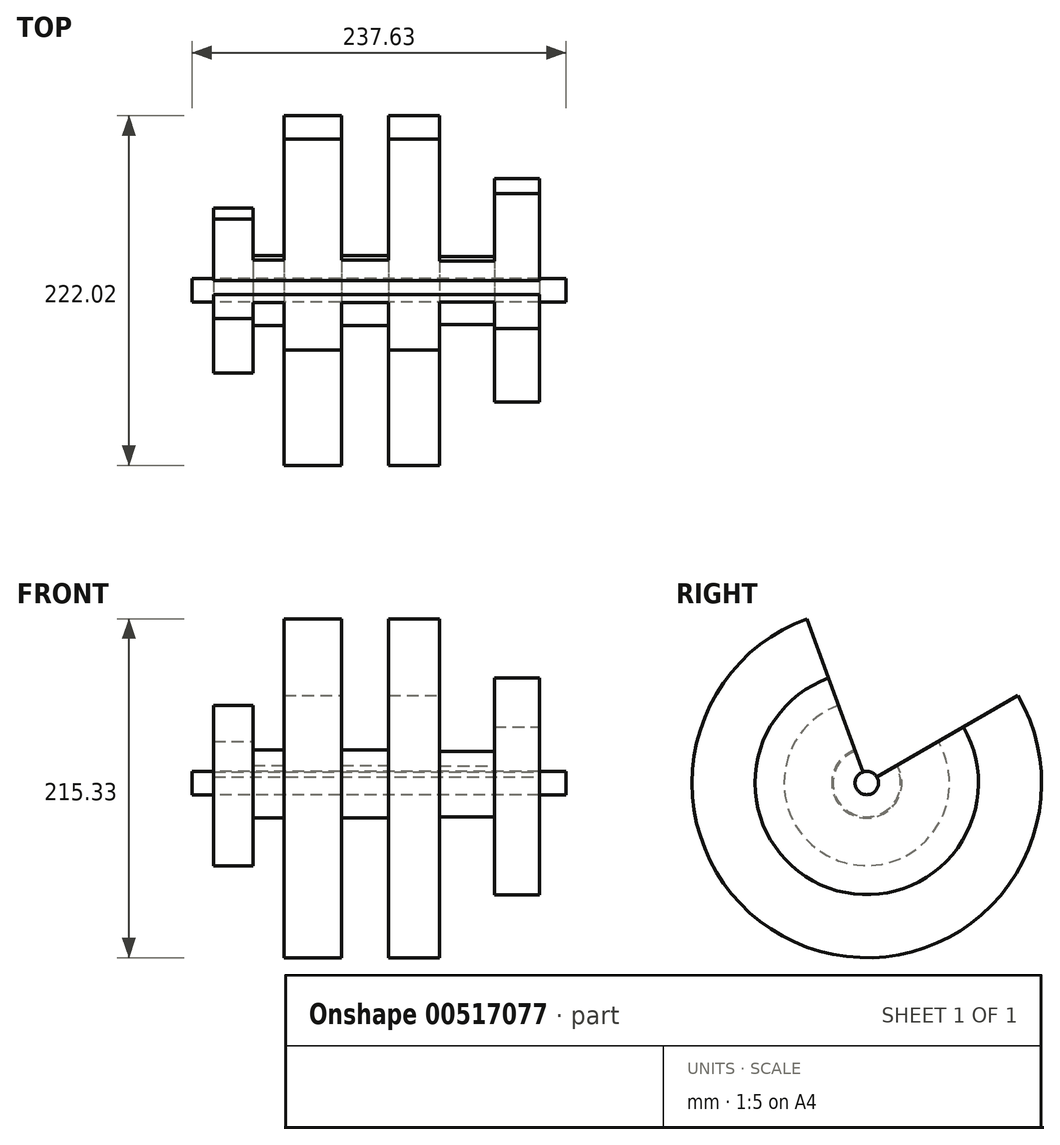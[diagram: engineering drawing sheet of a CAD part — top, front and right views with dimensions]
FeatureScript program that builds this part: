
annotation { "Feature Type Name" : "Feature", "Feature Type Description" : "" }
export const myFeature = defineFeature(function(context is Context, id is Id, definition is map)
    precondition{}
    {
        {
            var Q0;
            Q0=qCreatedBy(makeId("Front.planeOp"),FACE);
            var sketch = newSketch(context, id + "F0", { "sketchPlane" : qUnion([Q0])});
            skLineSegment(sketch, "E0.bottom", {"start": v(-116.02, 11.65) * mm, "end": v(121.6, 11.65) * mm});
            skLineSegment(sketch, "E0.top", {"start": v(-116.02, 4.2) * mm, "end": v(121.6, 4.2) * mm});
            skLineSegment(sketch, "E0.left", {"start": v(-116.02, 11.65) * mm, "end": v(-116.02, 4.2) * mm});
            skLineSegment(sketch, "E0.right", {"start": v(121.6, 11.65) * mm, "end": v(121.6, 4.2) * mm});
            skLineSegment(sketch, "E1", {"start": v(-102.16, 11.65) * mm, "end": v(-102.16, 56.7) * mm});
            skLineSegment(sketch, "E2", {"start": v(-102.16, 56.7) * mm, "end": v(-77.02, 56.7) * mm});
            skLineSegment(sketch, "E3", {"start": v(-77.02, 56.7) * mm, "end": v(-77.02, 26.46) * mm});
            skLineSegment(sketch, "E4", {"start": v(-77.02, 26.46) * mm, "end": v(-57.39, 26.46) * mm});
            skLineSegment(sketch, "E5", {"start": v(-57.39, 26.46) * mm, "end": v(-57.39, 115.2) * mm});
            skLineSegment(sketch, "E6", {"start": v(-57.39, 115.2) * mm, "end": v(-20.87, 115.2) * mm});
            skLineSegment(sketch, "E7", {"start": v(-20.87, 115.2) * mm, "end": v(-20.87, 26.46) * mm});
            skLineSegment(sketch, "E8", {"start": v(-20.87, 26.46) * mm, "end": v(8.97, 26.46) * mm});
            skLineSegment(sketch, "E9", {"start": v(8.97, 26.46) * mm, "end": v(8.97, 115.2) * mm});
            skLineSegment(sketch, "E10", {"start": v(8.97, 115.2) * mm, "end": v(41.17, 115.2) * mm});
            skLineSegment(sketch, "E11", {"start": v(41.17, 115.2) * mm, "end": v(41.17, 25.67) * mm});
            skLineSegment(sketch, "E12", {"start": v(41.17, 25.67) * mm, "end": v(76.12, 25.67) * mm});
            skLineSegment(sketch, "E13", {"start": v(76.12, 25.67) * mm, "end": v(76.12, 75.15) * mm});
            skLineSegment(sketch, "E14", {"start": v(76.12, 75.15) * mm, "end": v(104.79, 75.15) * mm});
            skLineSegment(sketch, "E15", {"start": v(104.79, 75.15) * mm, "end": v(104.79, 11.65) * mm});
            skSolve(sketch);
        }
        {
            var Q0;
            Q0=makeQuery(id+"F0.imprint","IMPRINT",FACE,{"disambiguationData":[TD([[makeQuery(id+"F0.imprint","IMPRINT",EDGE,{"derivedFrom":sQuery(id+"F0.wireOp",EDGE,"E0.bottom")}),-1.0]])]});
            var Q1;
            Q1=sQuery(id+"F0.wireOp",EDGE,"E0.top");
            revolve(context, id + "F1", {"entities" : qUnion([Q0]), "axis" : qUnion([Q1]), "revolveType" : RevolveType.FULL});
        }
        {
            var Q0;
            {var subQ0=sQuery(id+"F0.wireOp",EDGE,"E1");Q0=makeQuery(id+"F0.imprint","IMPRINT",FACE,{"disambiguationData":[TD([[makeQuery(id+"F0.imprint","IMPRINT",EDGE,{"derivedFrom":subQ0}),-1.0]])]});}
            var Q1;
            Q1=makeQuery(id+"F1.opRevolve","SWEPT_FACE",FACE,{"disambiguationData":[OSD([sQuery(id+"F0.wireOp",EDGE,"E0.bottom")])]});
            revolve(context, id + "F2", {"entities" : qUnion([Q0]), "axis" : qUnion([Q1]), "revolveType" : RevolveType.TWO_DIRECTIONS, "oppositeDirection" : true, "angle" : 300 * degree, "angleBack" : 20 * degree});
        }
    });
